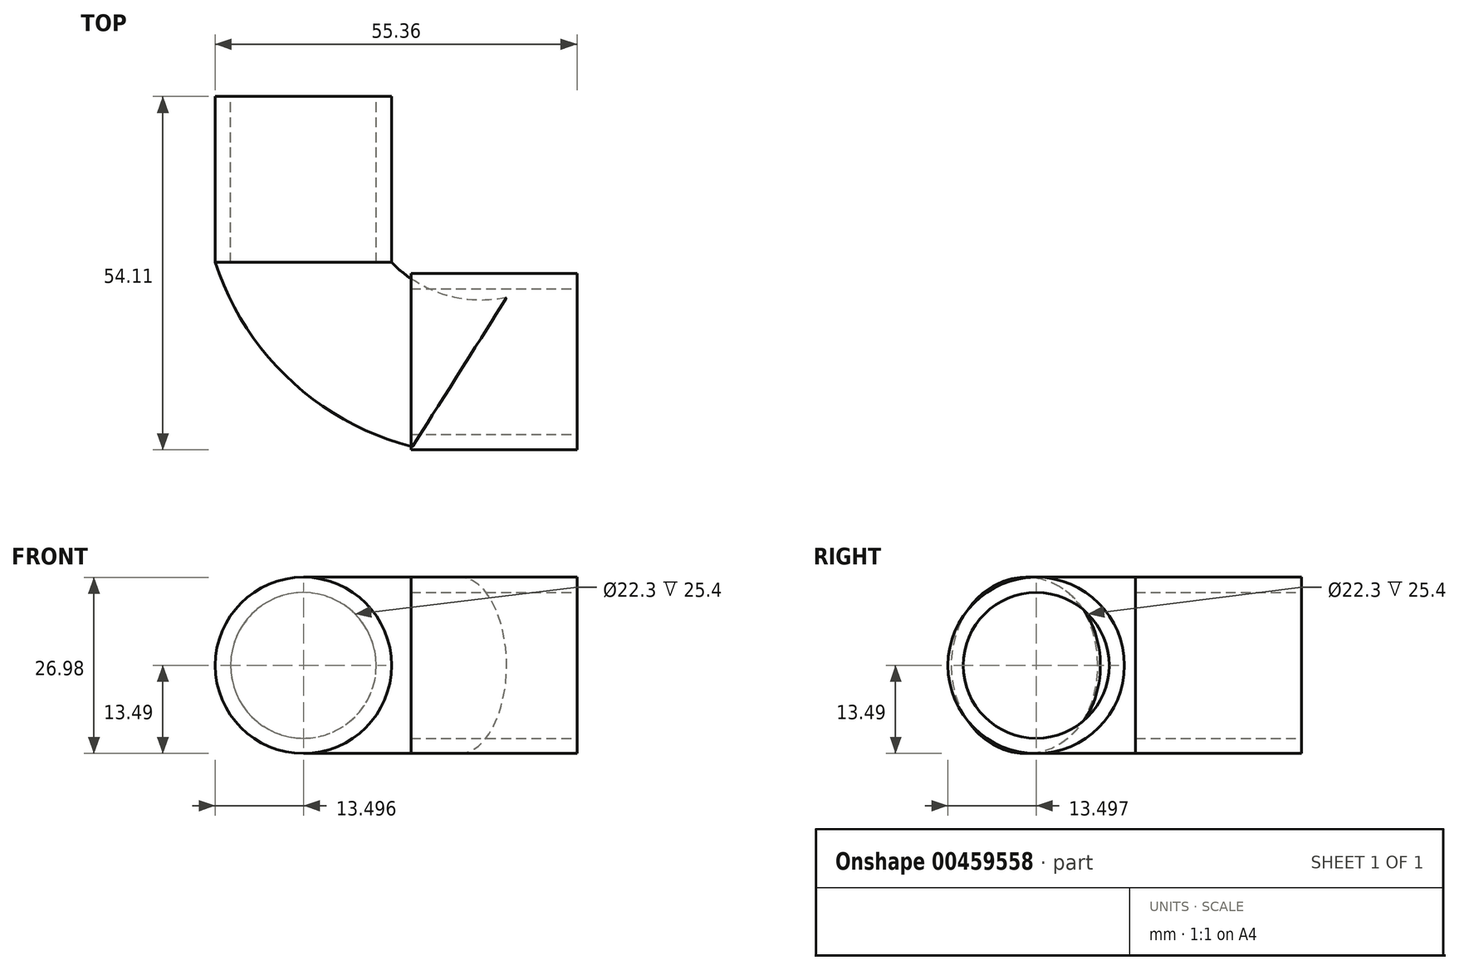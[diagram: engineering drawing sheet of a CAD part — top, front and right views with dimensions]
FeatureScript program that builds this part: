
annotation { "Feature Type Name" : "Feature", "Feature Type Description" : "" }
export const myFeature = defineFeature(function(context is Context, id is Id, definition is map)
    precondition{}
    {
        {
            var Q0;
            Q0=qCreatedBy(makeId("Right.planeOp"),FACE);
            var sketch = newSketch(context, id + "F0", { "sketchPlane" : qUnion([Q0])});
            skCircle(sketch, "E0", {"center": v(-15.21, 0) * mm, "radius": 13.5 * mm});
            skPoint(sketch, "E0.first.point", {"position": v(-2.5, 4.55) * mm});
            skPoint(sketch, "E0.second.point", {"position": v(-28.6, 1.69) * mm});
            skPoint(sketch, "E0.third.point", {"position": v(-28.7, 0.48) * mm});
            skSolve(sketch);
        }
        {
            var Q0;
            Q0=makeQuery(id+"F0.imprint","IMPRINT",FACE,{"disambiguationData":[TD([[makeQuery(id+"F0.imprint","IMPRINT",EDGE,{"derivedFrom":sQuery(id+"F0.wireOp",EDGE,"E0")}),1.0]])]});
            extrude(context, id + "F1", {"entities" : qUnion([Q0]), "depth" : 25.4 * mm});
        }
        {
            var Q0;
            Q0=qCreatedBy(makeId("Front.planeOp"),FACE);
            var sketch = newSketch(context, id + "F2", { "sketchPlane" : qUnion([Q0])});
            skCircle(sketch, "E1", {"center": v(-16.46, 0) * mm, "radius": 13.5 * mm});
            skPoint(sketch, "E1.first.point", {"position": v(-18.9, -13.27) * mm});
            skPoint(sketch, "E1.second.point", {"position": v(-15.77, -13.48) * mm});
            skPoint(sketch, "E1.third.point", {"position": v(-20.9, -12.74) * mm});
            skPoint(sketch, "E2", {"position": v(-24.5, -10.84) * mm});
            skPoint(sketch, "E3", {"position": v(0, 0) * mm});
            skSolve(sketch);
        }
        {
            var Q0;
            Q0=qSketchRegion(id+"F2",true);
            var Q1;
            Q1=qCreatedBy(makeId("Top.planeOp"),FACE);
            extrude(context, id + "F3", {"entities" : qUnion([Q0]), "oppositeDirection" : true, "endBoundEntityFace" : qUnion([Q1]), "depth" : 25.4 * mm});
        }
        {
            var Q0;
            Q0=makeQuery(id+"F3.opExtrude","CAP_FACE",FACE,{"disambiguationData":[OSD([sQuery(id+"F2.wireOp",EDGE,"E1")])],"isStart":true});
            var sketch = newSketch(context, id + "F4", { "sketchPlane" : qUnion([Q0])});
            skPoint(sketch, "E4", {"position": v(-17.05, 13.48) * mm});
            skSolve(sketch);
        }
        {
            var Q0;
            Q0=makeQuery(id+"F1.opExtrude","CAP_FACE",FACE,{"disambiguationData":[OSD([sQuery(id+"F0.wireOp",EDGE,"E0")])],"isStart":false});
            var sketch = newSketch(context, id + "F5", { "sketchPlane" : qUnion([Q0])});
            skCircle(sketch, "E5", {"center": v(-15.21, 0) * mm, "radius": 11.15 * mm});
            skSolve(sketch);
        }
        {
            var Q0;
            Q0=makeQuery(id+"F5.imprint","IMPRINT",FACE,{"disambiguationData":[TD([[makeQuery(id+"F5.imprint","IMPRINT",EDGE,{"derivedFrom":sQuery(id+"F5.wireOp",EDGE,"E5")}),1.0]])]});
            extrude(context, id + "F6", {"entities" : qUnion([Q0]), "operationType" : NewBodyOperationType.REMOVE, "oppositeDirection" : true, "depth" : 46.74 * mm});
        }
        {
            var Q0;
            Q0=makeQuery(id+"F3.opExtrude","CAP_FACE",FACE,{"disambiguationData":[OSD([sQuery(id+"F2.wireOp",EDGE,"E1")])],"isStart":false});
            var sketch = newSketch(context, id + "F7", { "sketchPlane" : qUnion([Q0])});
            skCircle(sketch, "E6", {"center": v(16.46, 0) * mm, "radius": 11.15 * mm});
            skSolve(sketch);
        }
        {
            var Q0;
            Q0=qSketchRegion(id+"F7",true);
            extrude(context, id + "F8", {"entities" : qUnion([Q0]), "operationType" : NewBodyOperationType.REMOVE, "oppositeDirection" : true, "depth" : 50.8 * mm});
        }
        {
            var Q0;
            Q0=qCreatedBy(makeId("Top.planeOp"),FACE);
            var sketch = newSketch(context, id + "F9", { "sketchPlane" : qUnion([Q0])});
            skPoint(sketch, "E7", {"position": v(0, -28.56) * mm});
            skPoint(sketch, "E8", {"position": v(-30.36, 0) * mm});
            skArc(sketch, "E9", {"start": v(-30.36, 0) * mm, "mid": v(-18.86, -18.19) * mm, "end": v(0, -28.56) * mm});
            skSolve(sketch);
        }
        {
            var Q0;
            Q0=makeQuery(id+"F4.imprint","IMPRINT",FACE,{"disambiguationData":[TD([[makeQuery(id+"F4.imprint","IMPRINT",EDGE,{"derivedFrom":makeQuery(id+"F3.opExtrude","CAP_EDGE",EDGE,{"disambiguationData":[OSD([sQuery(id+"F2.wireOp",EDGE,"E1")])],"isStart":true})}),1.0]])]});
            var Q1;
            Q1=sQuery(id+"F9.wireOp",EDGE,"E9");
            sweep(context, id + "F10", {"profiles" : qUnion([Q0]), "path" : qUnion([Q1])});
        }
    });
